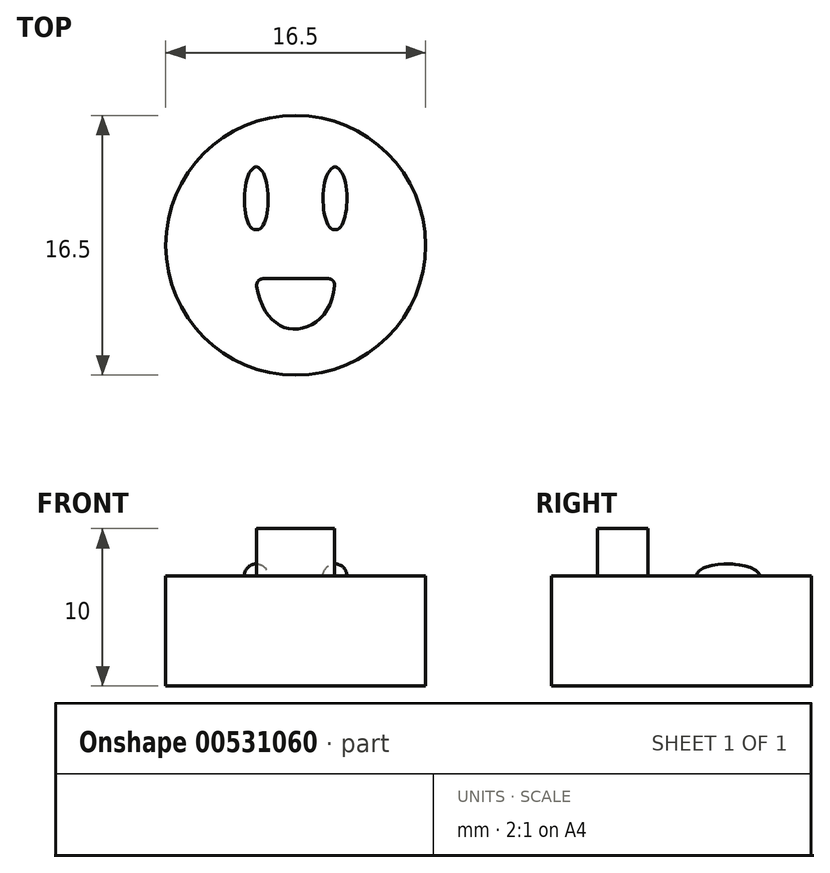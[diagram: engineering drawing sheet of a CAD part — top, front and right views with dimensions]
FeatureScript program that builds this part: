
annotation { "Feature Type Name" : "Feature", "Feature Type Description" : "" }
export const myFeature = defineFeature(function(context is Context, id is Id, definition is map)
    precondition{}
    {
        {
            var Q0;
            Q0=qCreatedBy(makeId("Top.planeOp"),FACE);
            var sketch = newSketch(context, id + "F0", { "sketchPlane" : qUnion([Q0])});
            skCircle(sketch, "E0", {"center": v(0, 0) * mm, "radius": 8.25 * mm});
            skSolve(sketch);
        }
        {
            var Q0;
            Q0 = qSketchRegion(id + "F0", true);
            extrude(context, id + "F1", {"entities" : qUnion([Q0]), "depth" : 7 * mm, "offsetDistance" : 25 * mm});
        }
        {
            var Q0;
            Q0=makeQuery(id+"F1.opExtrude","CAP_FACE",FACE,{"disambiguationData":[OSD([sQuery(id+"F0.wireOp",EDGE,"E0")])],"isStart":false});
            var sketch = newSketch(context, id + "F2", { "sketchPlane" : qUnion([Q0])});
            skLineSegment(sketch, "E1", {"start": v(-2.5, 5) * mm, "end": v(-2.5, 1) * mm});
            skLineSegment(sketch, "E2", {"start": v(-2.07, -2.13) * mm, "end": v(2.08, -2.13) * mm});
            skFitSpline(sketch, "E3", {"points": [v(-2.52, -2.13) * mm, v(0, -5.33) * mm, v(2.48, -2.13) * mm], "startDerivative": vector(0.9, -12.7) * mm, "endDerivative": vector(-0.44, 12.02) * mm});
            skFitSpline(sketch, "E4", {"points": [v(-2.5, 1) * mm, v(-2.5, 5) * mm], "startDerivative": vector(-2.8, -0.45) * mm, "endDerivative": vector(3.26, 0.9) * mm});
            skLineSegment(sketch, "E5", {"start": v(2.5, 5) * mm, "end": v(2.5, 1) * mm});
            skFitSpline(sketch, "E6", {"points": [v(2.5, 1) * mm, v(2.5, 5) * mm], "startDerivative": vector(-2.8, -0.45) * mm, "endDerivative": vector(3.26, 0.9) * mm});
            skArc(sketch, "E7.filletArc", {"start": v(-2.07, -2.13) * mm, "mid": v(-2.37, -2.26) * mm, "end": v(-2.47, -2.58) * mm});
            skArc(sketch, "E8.filletArc", {"start": v(2.48, -2.55) * mm, "mid": v(2.37, -2.25) * mm, "end": v(2.08, -2.13) * mm});
            skSolve(sketch);
        }
        {
            var Q0;
            Q0=makeQuery(id+"F2.imprint","IMPRINT",FACE,{"disambiguationData":[TD([[makeQuery(id+"F2.imprint","IMPRINT",EDGE,{"derivedFrom":sQuery(id+"F2.wireOp",EDGE,"E1")}),-1.0]])]});
            var Q1;
            Q1=sQuery(id+"F2.wireOp",EDGE,"E1");
            revolve(context, id + "F3", {"operationType" : NewBodyOperationType.ADD, "entities" : qUnion([Q0]), "axis" : qUnion([Q1]), "revolveType" : RevolveType.FULL});
        }
        {
            var Q0;
            Q0=makeQuery(id+"F2.imprint","IMPRINT",FACE,{"disambiguationData":[TD([[makeQuery(id+"F2.imprint","IMPRINT",EDGE,{"derivedFrom":sQuery(id+"F2.wireOp",EDGE,"E5")}),-1.0]])]});
            var Q1;
            Q1=sQuery(id+"F2.wireOp",EDGE,"E5");
            revolve(context, id + "F4", {"operationType" : NewBodyOperationType.ADD, "entities" : qUnion([Q0]), "axis" : qUnion([Q1]), "revolveType" : RevolveType.FULL});
        }
        {
            var Q0;
            Q0=makeQuery(id+"F2.imprint","IMPRINT",FACE,{"disambiguationData":[TD([[makeQuery(id+"F2.imprint","IMPRINT",EDGE,{"derivedFrom":sQuery(id+"F2.wireOp",EDGE,"E2")}),-1.0]])]});
            extrude(context, id + "F5", {"entities" : qUnion([Q0]), "operationType" : NewBodyOperationType.ADD, "depth" : 3 * mm, "offsetDistance" : 25 * mm});
        }
    });
